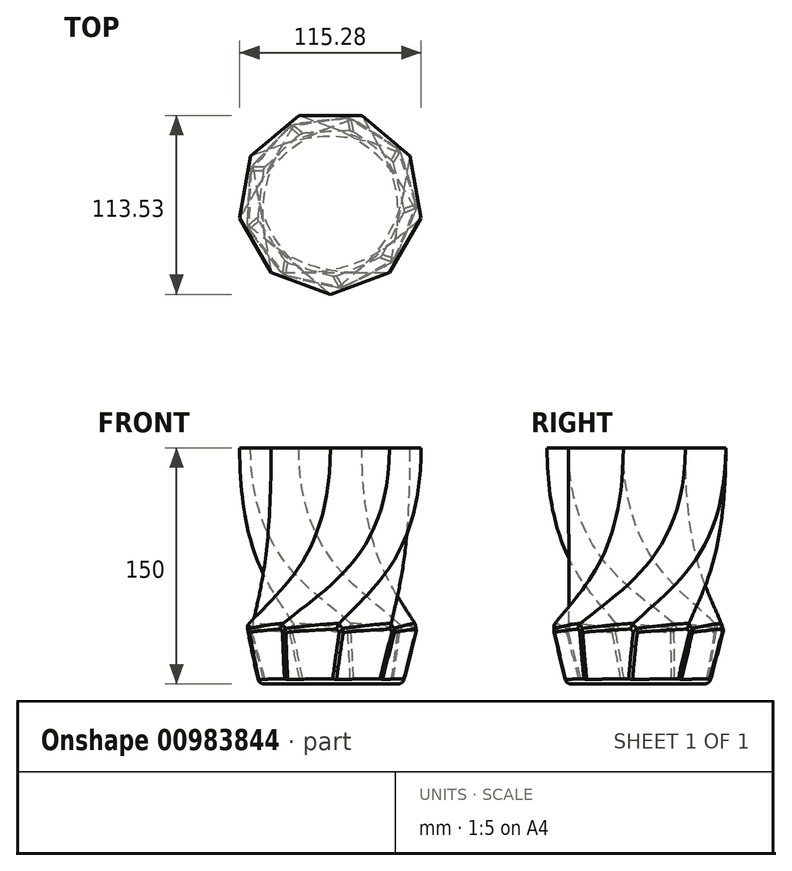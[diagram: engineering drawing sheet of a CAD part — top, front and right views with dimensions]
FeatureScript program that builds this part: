
annotation { "Feature Type Name" : "Feature", "Feature Type Description" : "" }
export const myFeature = defineFeature(function(context is Context, id is Id, definition is map)
    precondition{}
    {
        {
            assignVariable(context, id + "F0", {"name" : "h", "anyValue" : 150});
        }
        {
            var Q0;
            Q0=qCreatedBy(makeId("Top.planeOp"),FACE);
            var sketch = newSketch(context, id + "F1", { "sketchPlane" : qUnion([Q0])});
            skCircle(sketch, "E0.cCircle", {"center": v(0, 0) * mm, "radius": 65 * mm, "construction": true});
            skLineSegment(sketch, "E0.0", {"start": v(65, 23.66) * mm, "end": v(65, -23.66) * mm});
            skLineSegment(sketch, "E0.1", {"start": v(65, -23.66) * mm, "end": v(34.59, -59.9) * mm});
            skLineSegment(sketch, "E0.2", {"start": v(34.59, -59.9) * mm, "end": v(-12.01, -68.12) * mm});
            skLineSegment(sketch, "E0.3", {"start": v(-12.01, -68.12) * mm, "end": v(-52.99, -44.46) * mm});
            skLineSegment(sketch, "E0.4", {"start": v(-52.99, -44.46) * mm, "end": v(-69.17, 0) * mm});
            skLineSegment(sketch, "E0.5", {"start": v(-69.17, 0) * mm, "end": v(-52.99, 44.46) * mm});
            skLineSegment(sketch, "E0.6", {"start": v(-52.99, 44.46) * mm, "end": v(-12.01, 68.12) * mm});
            skLineSegment(sketch, "E0.7", {"start": v(-12.01, 68.12) * mm, "end": v(34.59, 59.9) * mm});
            skLineSegment(sketch, "E0.8", {"start": v(34.59, 59.9) * mm, "end": v(65, 23.66) * mm});
            skPoint(sketch, "E0.0.midPoint", {"position": v(65, 0) * mm});
            skSolve(sketch);
        }
        {
            var Q0;
            Q0=qCreatedBy(makeId("Top.planeOp"),FACE);
            cPlane(context, id + "F2", {"entities" : qUnion([Q0]), "cplaneType" : CPlaneType.OFFSET, "offset" : (getVariable(context, 'h')) * mm, "width" : 150 * mm, "height" : 150 * mm});
        }
        {
            var Q0;
            Q0=qCreatedBy(id+"F2.planeOp",FACE);
            var sketch = newSketch(context, id + "F3", { "sketchPlane" : qUnion([Q0])});
            skCircle(sketch, "E1.cCircle", {"center": v(0, 0) * mm, "radius": 55 * mm, "construction": true});
            skLineSegment(sketch, "E1.0", {"start": v(-20.02, 55) * mm, "end": v(20.02, 55) * mm});
            skLineSegment(sketch, "E1.1", {"start": v(20.02, 55) * mm, "end": v(50.69, 29.26) * mm});
            skLineSegment(sketch, "E1.2", {"start": v(50.69, 29.26) * mm, "end": v(57.64, -10.16) * mm});
            skLineSegment(sketch, "E1.3", {"start": v(57.64, -10.16) * mm, "end": v(37.62, -44.84) * mm});
            skLineSegment(sketch, "E1.4", {"start": v(37.62, -44.84) * mm, "end": v(0, -58.53) * mm});
            skLineSegment(sketch, "E1.5", {"start": v(0, -58.53) * mm, "end": v(-37.62, -44.84) * mm});
            skLineSegment(sketch, "E1.6", {"start": v(-37.62, -44.84) * mm, "end": v(-57.64, -10.16) * mm});
            skLineSegment(sketch, "E1.7", {"start": v(-57.64, -10.16) * mm, "end": v(-50.69, 29.26) * mm});
            skLineSegment(sketch, "E1.8", {"start": v(-50.69, 29.26) * mm, "end": v(-20.02, 55) * mm});
            skPoint(sketch, "E1.0.midPoint", {"position": v(0, 55) * mm});
            skSolve(sketch);
        }
        {
            var Q0;
            Q0=makeQuery(id+"F1.imprint","IMPRINT",FACE,{"disambiguationData":[TD([[makeQuery(id+"F1.imprint","IMPRINT",EDGE,{"derivedFrom":sQuery(id+"F1.wireOp",EDGE,"E0.0")}),-1.0]])]});
            var Q1;
            Q1=makeQuery(id+"F3.imprint","IMPRINT",FACE,{"disambiguationData":[TD([[makeQuery(id+"F3.imprint","IMPRINT",EDGE,{"derivedFrom":sQuery(id+"F3.wireOp",EDGE,"E1.0")}),-1.0]])]});
            var Q2;
            Q2=sQuery(id+"F1.wireOp",VERTEX,"E0.6.end");
            var Q3;
            Q3=sQuery(id+"F3.wireOp",VERTEX,"E1.6.end");
            loft(context, id + "F4", {"startCondition" : LoftEndDerivativeType.NORMAL_TO_PROFILE, "startMagnitude" : 1, "endCondition" : LoftEndDerivativeType.NORMAL_TO_PROFILE, "endMagnitude" : 2, "sheetProfilesArray" : [{ "sheetProfileEntities" : qUnion([Q0]) }, { "sheetProfileEntities" : qUnion([Q1]) }], "matchConnections" : true, "connections" : [{ "connectionEntities" : qUnion([Q2, Q3]), "connectionEdgeQueries" : qUnion([]), "connectionEdgeParameters" : [] }]});
        }
        {
            var Q0;
            Q0=makeQuery(id+"F4.opLoft","CAP_FACE",FACE,{"disambiguationData":[OSD([makeQuery(id+"F1.imprint","IMPRINT",FACE,{"disambiguationData":[TD([[makeQuery(id+"F1.imprint","IMPRINT",EDGE,{"derivedFrom":sQuery(id+"F1.wireOp",EDGE,"E0.0")}),-1.0]])]})])],"isStart":true});
            chamfer(context, id + "F5", {"entities" : qUnion([Q0]), "chamferType" : ChamferType.TWO_OFFSETS, "width1" : 30 * mm, "oppositeDirection" : false, "width2" : 10 * mm, "tangentPropagation" : true});
        }
        {
            var Q0;
            Q0=makeQuery(id+"F5.opChamfer","BLEND_FACE",FACE,{"disambiguationData":[OSD([sQuery(id+"F1.wireOp",EDGE,"E0.0"),sQuery(id+"F1.wireOp",EDGE,"E0.1"),sQuery(id+"F1.wireOp",EDGE,"E0.8")])]});
            var Q1;
            Q1=makeQuery(id+"F5.opChamfer","BLEND_FACE",FACE,{"disambiguationData":[OSD([sQuery(id+"F1.wireOp",EDGE,"E0.0"),sQuery(id+"F1.wireOp",EDGE,"E0.7"),sQuery(id+"F1.wireOp",EDGE,"E0.8")])]});
            var Q2;
            Q2=makeQuery(id+"F5.opChamfer","BLEND_FACE",FACE,{"disambiguationData":[OSD([sQuery(id+"F1.wireOp",EDGE,"E0.6"),sQuery(id+"F1.wireOp",EDGE,"E0.7"),sQuery(id+"F1.wireOp",EDGE,"E0.8")])]});
            var Q3;
            Q3=makeQuery(id+"F5.opChamfer","BLEND_FACE",FACE,{"disambiguationData":[OSD([sQuery(id+"F1.wireOp",EDGE,"E0.5"),sQuery(id+"F1.wireOp",EDGE,"E0.6"),sQuery(id+"F1.wireOp",EDGE,"E0.7")])]});
            var Q4;
            Q4=makeQuery(id+"F5.opChamfer","BLEND_FACE",FACE,{"disambiguationData":[OSD([sQuery(id+"F1.wireOp",EDGE,"E0.4"),sQuery(id+"F1.wireOp",EDGE,"E0.5"),sQuery(id+"F1.wireOp",EDGE,"E0.6")])]});
            var Q5;
            Q5=makeQuery(id+"F5.opChamfer","BLEND_FACE",FACE,{"disambiguationData":[OSD([sQuery(id+"F1.wireOp",EDGE,"E0.3"),sQuery(id+"F1.wireOp",EDGE,"E0.4"),sQuery(id+"F1.wireOp",EDGE,"E0.5")])]});
            var Q6;
            Q6=makeQuery(id+"F5.opChamfer","BLEND_FACE",FACE,{"disambiguationData":[OSD([sQuery(id+"F1.wireOp",EDGE,"E0.2"),sQuery(id+"F1.wireOp",EDGE,"E0.3"),sQuery(id+"F1.wireOp",EDGE,"E0.4")])]});
            var Q7;
            Q7=makeQuery(id+"F5.opChamfer","BLEND_FACE",FACE,{"disambiguationData":[OSD([sQuery(id+"F1.wireOp",EDGE,"E0.1"),sQuery(id+"F1.wireOp",EDGE,"E0.2"),sQuery(id+"F1.wireOp",EDGE,"E0.3")])]});
            var Q8;
            Q8=makeQuery(id+"F5.opChamfer","BLEND_FACE",FACE,{"disambiguationData":[OSD([sQuery(id+"F1.wireOp",EDGE,"E0.0"),sQuery(id+"F1.wireOp",EDGE,"E0.1"),sQuery(id+"F1.wireOp",EDGE,"E0.2")])]});
            fillet(context, id + "F6", {"entities" : qUnion([Q0, Q1, Q2, Q3, Q4, Q5, Q6, Q7, Q8]), "radius" : 4 * mm, "tangentPropagation" : true, "allowEdgeOverflow" : false});
        }
        {
            var Q0;
            Q0=qCreatedBy(makeId("Front.planeOp"),FACE);
            cPlane(context, id + "F7", {"entities" : qUnion([Q0]), "cplaneType" : CPlaneType.OFFSET, "offset" : 100 * mm, "width" : 150 * mm, "height" : 150 * mm});
        }
    });
